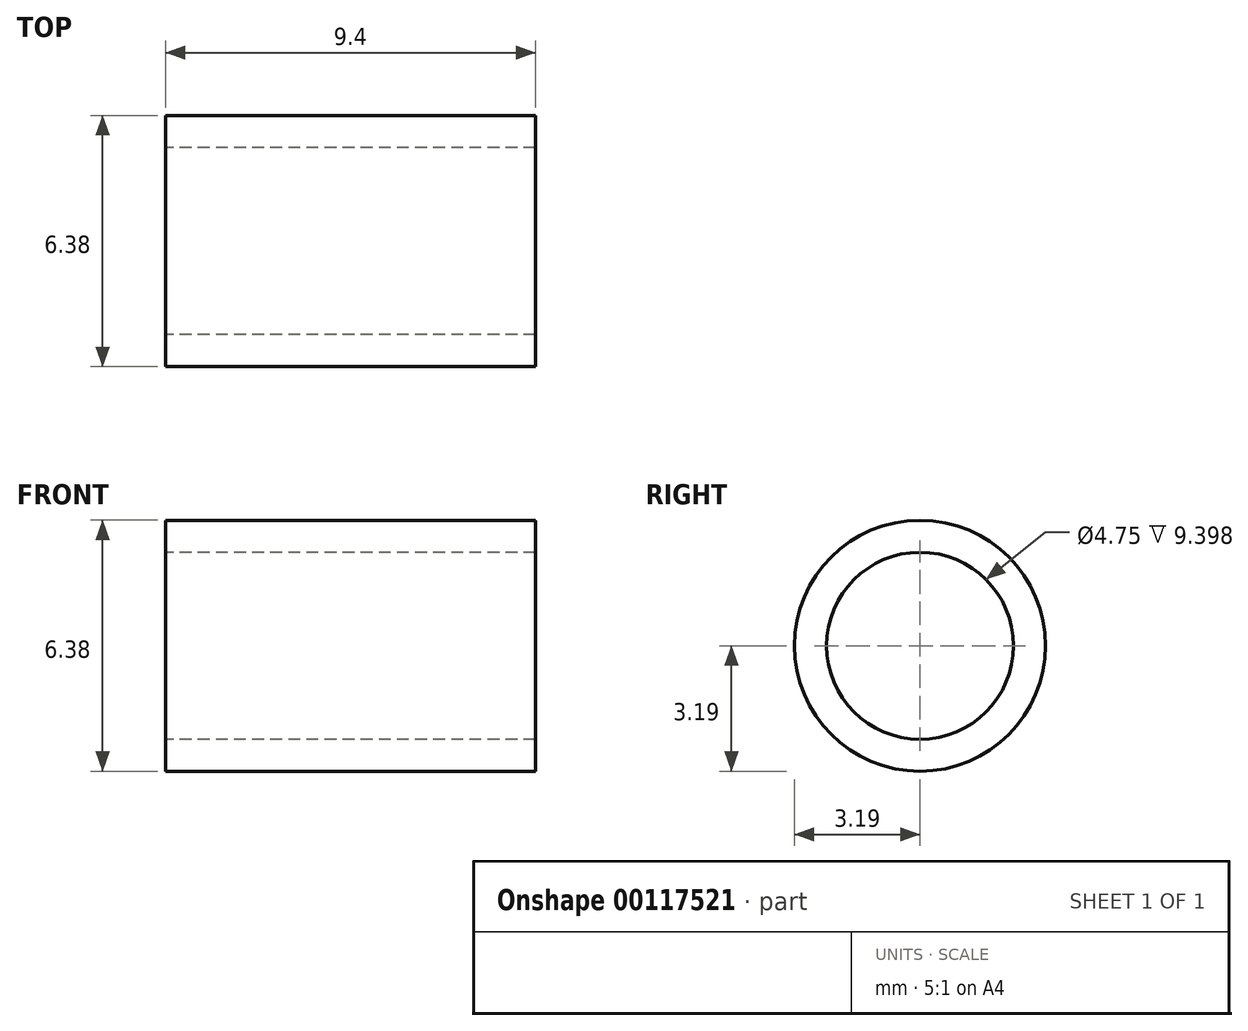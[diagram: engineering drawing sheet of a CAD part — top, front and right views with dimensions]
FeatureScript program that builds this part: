
annotation { "Feature Type Name" : "Feature", "Feature Type Description" : "" }
export const myFeature = defineFeature(function(context is Context, id is Id, definition is map)
    precondition{}
    {
        {
            var Q0;
            Q0=qCreatedBy(makeId("Right.planeOp"),FACE);
            var sketch = newSketch(context, id + "F0", { "sketchPlane" : qUnion([Q0])});
            skCircle(sketch, "E0", {"center": v(0, 0) * mm, "radius": 3.19 * mm});
            skSolve(sketch);
        }
        {
            var Q0;
            Q0 = qSketchRegion(id + "F0", true);
            extrude(context, id + "F1", {"entities" : qUnion([Q0]), "depth" : 9.4 * mm, "symmetric" : true});
        }
        {
            var Q0;
            Q0=makeQuery(id+"F1.opExtrude","CAP_FACE",FACE,{"disambiguationData":[OSD([sQuery(id+"F0.wireOp",EDGE,"E0")])],"isStart":true});
            var sketch = newSketch(context, id + "F2", { "sketchPlane" : qUnion([Q0])});
            skCircle(sketch, "E1", {"center": v(0, 0) * mm, "radius": 2.37 * mm});
            skSolve(sketch);
        }
        {
            var Q0;
            Q0 = qSketchRegion(id + "F2", true);
            extrude(context, id + "F3", {"entities" : qUnion([Q0]), "operationType" : NewBodyOperationType.REMOVE, "oppositeDirection" : true, "depth" : 25.4 * mm, "symmetric" : true});
        }
    });
